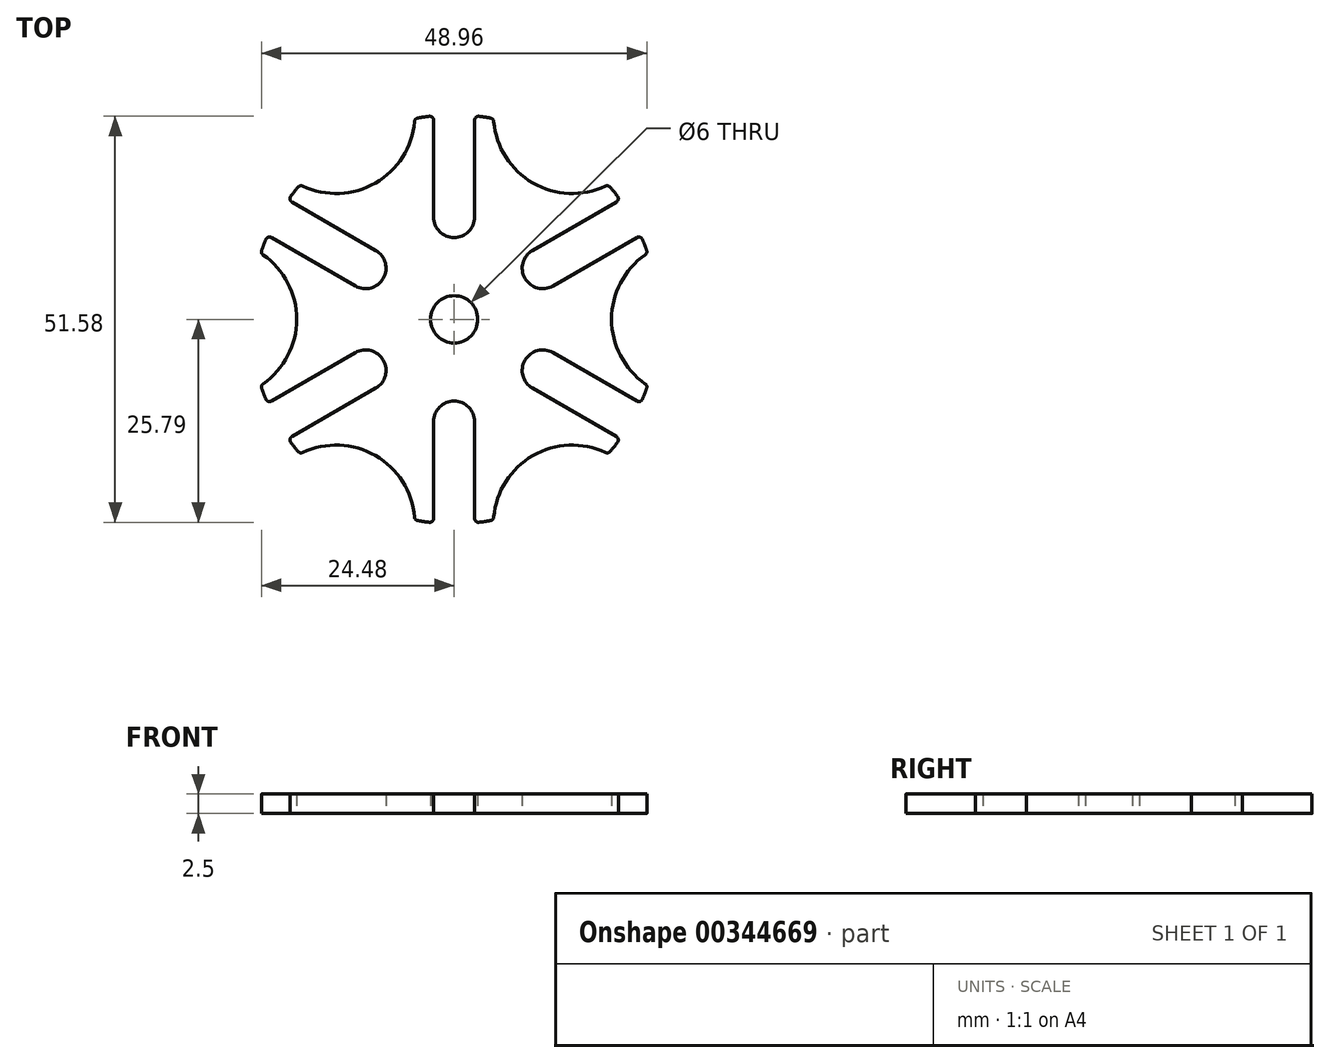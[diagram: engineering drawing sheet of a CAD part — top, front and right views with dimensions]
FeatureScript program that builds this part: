
annotation { "Feature Type Name" : "Feature", "Feature Type Description" : "" }
export const myFeature = defineFeature(function(context is Context, id is Id, definition is map)
    precondition{}
    {
        {
            var Q0;
            Q0=qCreatedBy(makeId("Top.planeOp"),FACE);
            var sketch = newSketch(context, id + "F0", { "sketchPlane" : qUnion([Q0])});
            skLineSegment(sketch, "E0", {"start": v(0, 0) * mm, "end": v(22.5, 13) * mm, "construction": true});
            skLineSegment(sketch, "E1", {"start": v(22.5, 13) * mm, "end": v(30, 0) * mm});
            skLineSegment(sketch, "E2", {"start": v(30, 0) * mm, "end": v(0, 0) * mm, "construction": true});
            skCircle(sketch, "E3", {"center": v(0, 0) * mm, "radius": 25.98 * mm, "construction": true});
            skLineSegment(sketch, "E4", {"start": v(30, 0) * mm, "end": v(20, 17.32) * mm, "construction": true});
            skLineSegment(sketch, "E5", {"start": v(20, 17.32) * mm, "end": v(20, 0) * mm, "construction": true});
            skLineSegment(sketch, "E6", {"start": v(21.09, 15.18) * mm, "end": v(9.95, 8.75) * mm});
            skLineSegment(sketch, "E7", {"start": v(23.69, 10.67) * mm, "end": v(12.55, 4.24) * mm});
            skArc(sketch, "E8", {"start": v(9.95, 8.75) * mm, "mid": v(9, 5.2) * mm, "end": v(12.55, 4.24) * mm});
            skArc(sketch, "E9", {"start": v(24.58, 8.4) * mm, "mid": v(20, 0) * mm, "end": v(24.58, -8.4) * mm});
            skArc(sketch, "E10", {"start": v(23.69, 10.67) * mm, "mid": v(24.16, 9.55) * mm, "end": v(24.58, 8.4) * mm});
            skArc(sketch, "E11.MirrorCS", {"start": v(21.09, 15.18) * mm, "mid": v(20.35, 16.15) * mm, "end": v(19.57, 17.09) * mm});
            skArc(sketch, "E12.1.0", {"start": v(-2.6, 25.85) * mm, "mid": v(-3.81, 25.7) * mm, "end": v(-5.01, 25.5) * mm});
            skLineSegment(sketch, "E12.1.1", {"start": v(-2.6, 25.85) * mm, "end": v(-2.6, 13) * mm});
            skArc(sketch, "E12.1.2", {"start": v(-2.6, 13) * mm, "mid": v(0, 10.4) * mm, "end": v(2.6, 13) * mm});
            skLineSegment(sketch, "E12.1.3", {"start": v(2.6, 25.85) * mm, "end": v(2.6, 13) * mm});
            skArc(sketch, "E12.1.4", {"start": v(2.6, 25.85) * mm, "mid": v(3.81, 25.7) * mm, "end": v(5.01, 25.5) * mm});
            skArc(sketch, "E12.1.5", {"start": v(5.01, 25.5) * mm, "mid": v(10, 17.32) * mm, "end": v(19.57, 17.09) * mm});
            skArc(sketch, "E12.2.0", {"start": v(-23.69, 10.67) * mm, "mid": v(-24.16, 9.55) * mm, "end": v(-24.58, 8.4) * mm});
            skLineSegment(sketch, "E12.2.1", {"start": v(-23.69, 10.67) * mm, "end": v(-12.55, 4.24) * mm});
            skArc(sketch, "E12.2.2", {"start": v(-12.55, 4.24) * mm, "mid": v(-9, 5.2) * mm, "end": v(-9.95, 8.75) * mm});
            skLineSegment(sketch, "E12.2.3", {"start": v(-21.09, 15.18) * mm, "end": v(-9.95, 8.75) * mm});
            skArc(sketch, "E12.2.4", {"start": v(-21.09, 15.18) * mm, "mid": v(-20.35, 16.15) * mm, "end": v(-19.57, 17.09) * mm});
            skArc(sketch, "E12.2.5", {"start": v(-19.57, 17.09) * mm, "mid": v(-10, 17.32) * mm, "end": v(-5.01, 25.5) * mm});
            skArc(sketch, "E12.3.0", {"start": v(-21.09, -15.18) * mm, "mid": v(-20.35, -16.15) * mm, "end": v(-19.57, -17.09) * mm});
            skLineSegment(sketch, "E12.3.1", {"start": v(-21.09, -15.18) * mm, "end": v(-9.95, -8.75) * mm});
            skArc(sketch, "E12.3.2", {"start": v(-9.95, -8.75) * mm, "mid": v(-9, -5.2) * mm, "end": v(-12.55, -4.24) * mm});
            skLineSegment(sketch, "E12.3.3", {"start": v(-23.69, -10.67) * mm, "end": v(-12.55, -4.24) * mm});
            skArc(sketch, "E12.3.4", {"start": v(-23.69, -10.67) * mm, "mid": v(-24.16, -9.55) * mm, "end": v(-24.58, -8.4) * mm});
            skArc(sketch, "E12.3.5", {"start": v(-24.58, -8.4) * mm, "mid": v(-20, 0) * mm, "end": v(-24.58, 8.4) * mm});
            skArc(sketch, "E12.4.0", {"start": v(2.6, -25.85) * mm, "mid": v(3.81, -25.7) * mm, "end": v(5.01, -25.5) * mm});
            skLineSegment(sketch, "E12.4.1", {"start": v(2.6, -25.85) * mm, "end": v(2.6, -13) * mm});
            skArc(sketch, "E12.4.2", {"start": v(2.6, -13) * mm, "mid": v(0, -10.4) * mm, "end": v(-2.6, -13) * mm});
            skLineSegment(sketch, "E12.4.3", {"start": v(-2.6, -25.85) * mm, "end": v(-2.6, -13) * mm});
            skArc(sketch, "E12.4.4", {"start": v(-2.6, -25.85) * mm, "mid": v(-3.81, -25.7) * mm, "end": v(-5.01, -25.5) * mm});
            skArc(sketch, "E12.4.5", {"start": v(-5.01, -25.5) * mm, "mid": v(-10, -17.32) * mm, "end": v(-19.57, -17.09) * mm});
            skCircle(sketch, "E13", {"center": v(0, 0) * mm, "radius": 3 * mm});
            skArc(sketch, "E14.2.5.0", {"start": v(23.69, -10.67) * mm, "mid": v(24.16, -9.55) * mm, "end": v(24.58, -8.4) * mm});
            skLineSegment(sketch, "E14.4.5.0", {"start": v(23.69, -10.67) * mm, "end": v(12.55, -4.24) * mm});
            skArc(sketch, "E14.7.5.0", {"start": v(12.55, -4.24) * mm, "mid": v(9, -5.2) * mm, "end": v(9.95, -8.75) * mm});
            skLineSegment(sketch, "E14.11.5.0", {"start": v(21.09, -15.18) * mm, "end": v(9.95, -8.75) * mm});
            skArc(sketch, "E14.14.5.0", {"start": v(21.09, -15.18) * mm, "mid": v(20.35, -16.15) * mm, "end": v(19.57, -17.09) * mm});
            skArc(sketch, "E14.18.5.0", {"start": v(19.57, -17.09) * mm, "mid": v(10, -17.32) * mm, "end": v(5.01, -25.5) * mm});
            skSolve(sketch);
        }
        {
            var Q0;
            Q0=makeQuery(id+"F0.imprint","IMPRINT",FACE,{"disambiguationData":[TD([[makeQuery(id+"F0.imprint","IMPRINT",EDGE,{"derivedFrom":sQuery(id+"F0.wireOp",EDGE,"E6")}),-1.0]])]});
            extrude(context, id + "F1", {"entities" : qUnion([Q0]), "depth" : 2.5 * mm});
        }
        {
            var Q0;
            Q0=makeQuery(id+"F1.opExtrude","SWEPT_EDGE",EDGE,{"disambiguationData":[OSD([sQuery(id+"F0.wireOp",EDGE,"E14.2.5.0"),sQuery(id+"F0.wireOp",EDGE,"E14.4.5.0")])]});
            var Q1;
            Q1=makeQuery(id+"F1.opExtrude","SWEPT_EDGE",EDGE,{"disambiguationData":[OSD([sQuery(id+"F0.wireOp",EDGE,"E14.11.5.0"),sQuery(id+"F0.wireOp",EDGE,"E14.14.5.0")])]});
            var Q2;
            Q2=makeQuery(id+"F1.opExtrude","SWEPT_EDGE",EDGE,{"disambiguationData":[OSD([sQuery(id+"F0.wireOp",EDGE,"E9"),sQuery(id+"F0.wireOp",EDGE,"E14.2.5.0")])]});
            var Q3;
            Q3=makeQuery(id+"F1.opExtrude","SWEPT_EDGE",EDGE,{"disambiguationData":[OSD([sQuery(id+"F0.wireOp",EDGE,"E14.14.5.0"),sQuery(id+"F0.wireOp",EDGE,"E14.18.5.0")])]});
            var Q4;
            Q4=makeQuery(id+"F1.opExtrude","SWEPT_EDGE",EDGE,{"disambiguationData":[OSD([sQuery(id+"F0.wireOp",EDGE,"E12.4.0"),sQuery(id+"F0.wireOp",EDGE,"E14.18.5.0")])]});
            var Q5;
            Q5=makeQuery(id+"F1.opExtrude","SWEPT_EDGE",EDGE,{"disambiguationData":[OSD([sQuery(id+"F0.wireOp",EDGE,"E12.4.0"),sQuery(id+"F0.wireOp",EDGE,"E12.4.1")])]});
            var Q6;
            Q6=makeQuery(id+"F1.opExtrude","SWEPT_EDGE",EDGE,{"disambiguationData":[OSD([sQuery(id+"F0.wireOp",EDGE,"E12.4.3"),sQuery(id+"F0.wireOp",EDGE,"E12.4.4")])]});
            var Q7;
            Q7=makeQuery(id+"F1.opExtrude","SWEPT_EDGE",EDGE,{"disambiguationData":[OSD([sQuery(id+"F0.wireOp",EDGE,"E12.4.4"),sQuery(id+"F0.wireOp",EDGE,"E12.4.5")])]});
            var Q8;
            Q8=makeQuery(id+"F1.opExtrude","SWEPT_EDGE",EDGE,{"disambiguationData":[OSD([sQuery(id+"F0.wireOp",EDGE,"E12.3.0"),sQuery(id+"F0.wireOp",EDGE,"E12.3.1")])]});
            var Q9;
            Q9=makeQuery(id+"F1.opExtrude","SWEPT_EDGE",EDGE,{"disambiguationData":[OSD([sQuery(id+"F0.wireOp",EDGE,"E12.3.0"),sQuery(id+"F0.wireOp",EDGE,"E12.4.5")])]});
            var Q10;
            Q10=makeQuery(id+"F1.opExtrude","SWEPT_EDGE",EDGE,{"disambiguationData":[OSD([sQuery(id+"F0.wireOp",EDGE,"E12.3.3"),sQuery(id+"F0.wireOp",EDGE,"E12.3.4")])]});
            var Q11;
            Q11=makeQuery(id+"F1.opExtrude","SWEPT_EDGE",EDGE,{"disambiguationData":[OSD([sQuery(id+"F0.wireOp",EDGE,"E12.3.4"),sQuery(id+"F0.wireOp",EDGE,"E12.3.5")])]});
            var Q12;
            Q12=makeQuery(id+"F1.opExtrude","SWEPT_EDGE",EDGE,{"disambiguationData":[OSD([sQuery(id+"F0.wireOp",EDGE,"E12.2.0"),sQuery(id+"F0.wireOp",EDGE,"E12.2.1")])]});
            var Q13;
            Q13=makeQuery(id+"F1.opExtrude","SWEPT_EDGE",EDGE,{"disambiguationData":[OSD([sQuery(id+"F0.wireOp",EDGE,"E12.2.0"),sQuery(id+"F0.wireOp",EDGE,"E12.3.5")])]});
            var Q14;
            Q14=makeQuery(id+"F1.opExtrude","SWEPT_EDGE",EDGE,{"disambiguationData":[OSD([sQuery(id+"F0.wireOp",EDGE,"E12.2.3"),sQuery(id+"F0.wireOp",EDGE,"E12.2.4")])]});
            var Q15;
            Q15=makeQuery(id+"F1.opExtrude","SWEPT_EDGE",EDGE,{"disambiguationData":[OSD([sQuery(id+"F0.wireOp",EDGE,"E12.2.4"),sQuery(id+"F0.wireOp",EDGE,"E12.2.5")])]});
            var Q16;
            Q16=makeQuery(id+"F1.opExtrude","SWEPT_EDGE",EDGE,{"disambiguationData":[OSD([sQuery(id+"F0.wireOp",EDGE,"E12.1.0"),sQuery(id+"F0.wireOp",EDGE,"E12.2.5")])]});
            var Q17;
            Q17=makeQuery(id+"F1.opExtrude","SWEPT_EDGE",EDGE,{"disambiguationData":[OSD([sQuery(id+"F0.wireOp",EDGE,"E12.1.0"),sQuery(id+"F0.wireOp",EDGE,"E12.1.1")])]});
            var Q18;
            Q18=makeQuery(id+"F1.opExtrude","SWEPT_EDGE",EDGE,{"disambiguationData":[OSD([sQuery(id+"F0.wireOp",EDGE,"E12.1.3"),sQuery(id+"F0.wireOp",EDGE,"E12.1.4")])]});
            var Q19;
            Q19=makeQuery(id+"F1.opExtrude","SWEPT_EDGE",EDGE,{"disambiguationData":[OSD([sQuery(id+"F0.wireOp",EDGE,"E12.1.4"),sQuery(id+"F0.wireOp",EDGE,"E12.1.5")])]});
            var Q20;
            Q20=makeQuery(id+"F1.opExtrude","SWEPT_EDGE",EDGE,{"disambiguationData":[OSD([sQuery(id+"F0.wireOp",EDGE,"E6"),sQuery(id+"F0.wireOp",EDGE,"E11.MirrorCS")])]});
            var Q21;
            Q21=makeQuery(id+"F1.opExtrude","SWEPT_EDGE",EDGE,{"disambiguationData":[OSD([sQuery(id+"F0.wireOp",EDGE,"E11.MirrorCS"),sQuery(id+"F0.wireOp",EDGE,"E12.1.5")])]});
            var Q22;
            Q22=makeQuery(id+"F1.opExtrude","SWEPT_EDGE",EDGE,{"disambiguationData":[OSD([sQuery(id+"F0.wireOp",EDGE,"E7"),sQuery(id+"F0.wireOp",EDGE,"E10")])]});
            var Q23;
            Q23=makeQuery(id+"F1.opExtrude","SWEPT_EDGE",EDGE,{"disambiguationData":[OSD([sQuery(id+"F0.wireOp",EDGE,"E9"),sQuery(id+"F0.wireOp",EDGE,"E10")])]});
            fillet(context, id + "F2", {"entities" : qUnion([Q0, Q1, Q2, Q3, Q4, Q5, Q6, Q7, Q8, Q9, Q10, Q11, Q12, Q13, Q14, Q15, Q16, Q17, Q18, Q19, Q20, Q21, Q22, Q23]), "radius" : 0.5 * mm, "tangentPropagation" : true, "allowEdgeOverflow" : false});
        }
    });
